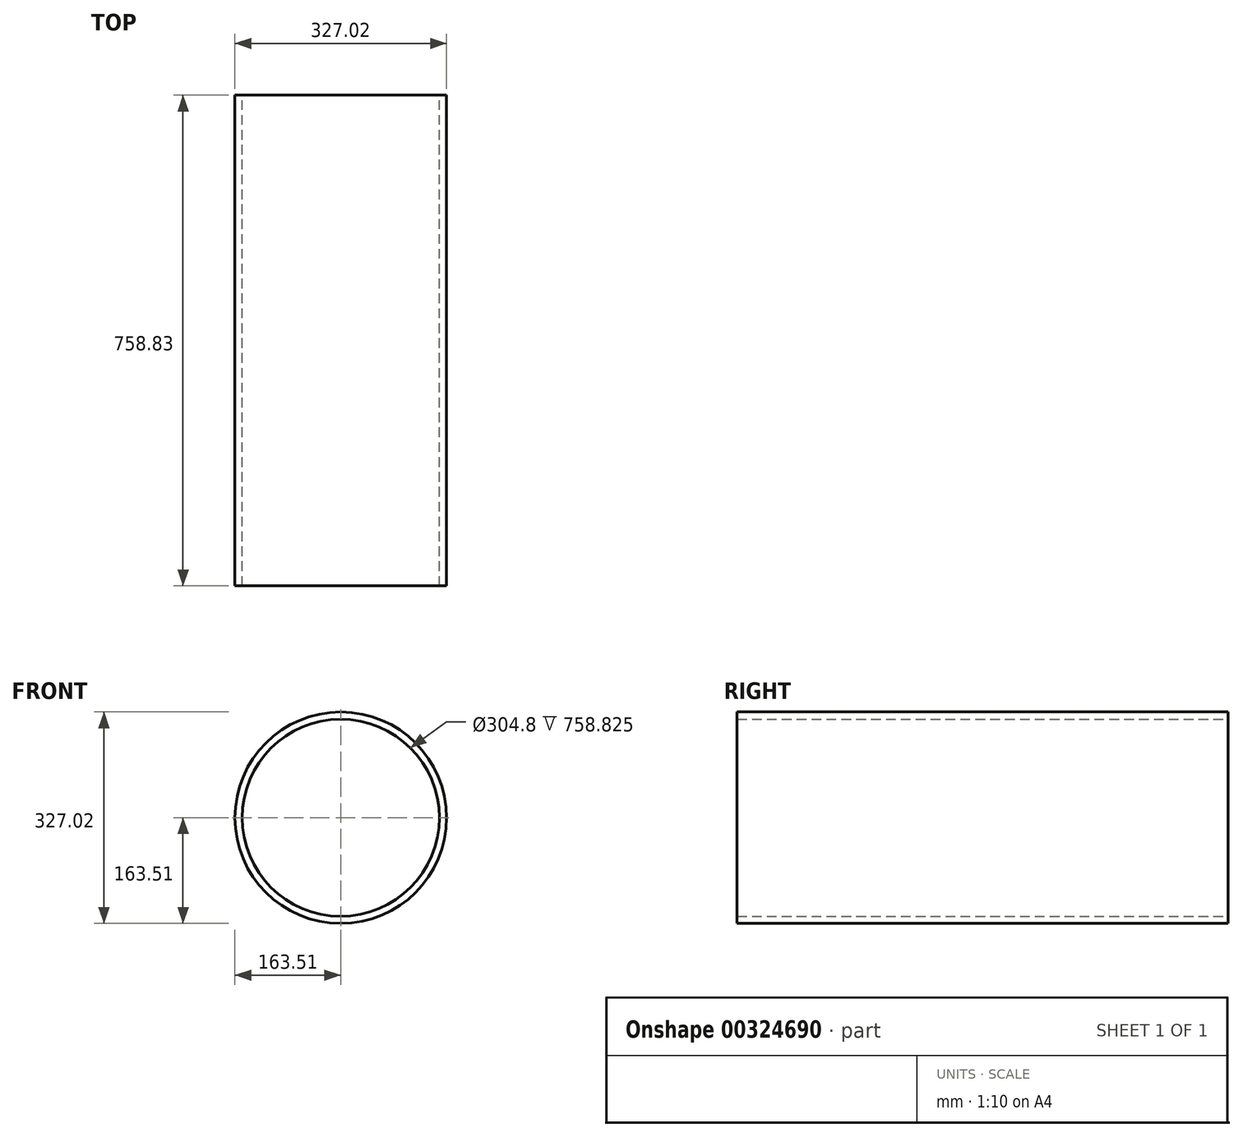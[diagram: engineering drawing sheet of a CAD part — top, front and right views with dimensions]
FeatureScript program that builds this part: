
annotation { "Feature Type Name" : "Feature", "Feature Type Description" : "" }
export const myFeature = defineFeature(function(context is Context, id is Id, definition is map)
    precondition{}
    {
        {
            var Q0;
            Q0=qCreatedBy(makeId("Front.planeOp"),FACE);
            var sketch = newSketch(context, id + "F0", { "sketchPlane" : qUnion([Q0])});
            skCircle(sketch, "E0", {"center": v(0, 0) * mm, "radius": 163.51 * mm});
            skCircle(sketch, "E1", {"center": v(0, 0) * mm, "radius": 152.4 * mm});
            skSolve(sketch);
        }
        {
            var Q0;
            Q0=qSketchRegion(id+"F0",true);
            extrude(context, id + "F1", {"entities" : qUnion([Q0]), "depth" : 758.82 * mm});
        }
    });
